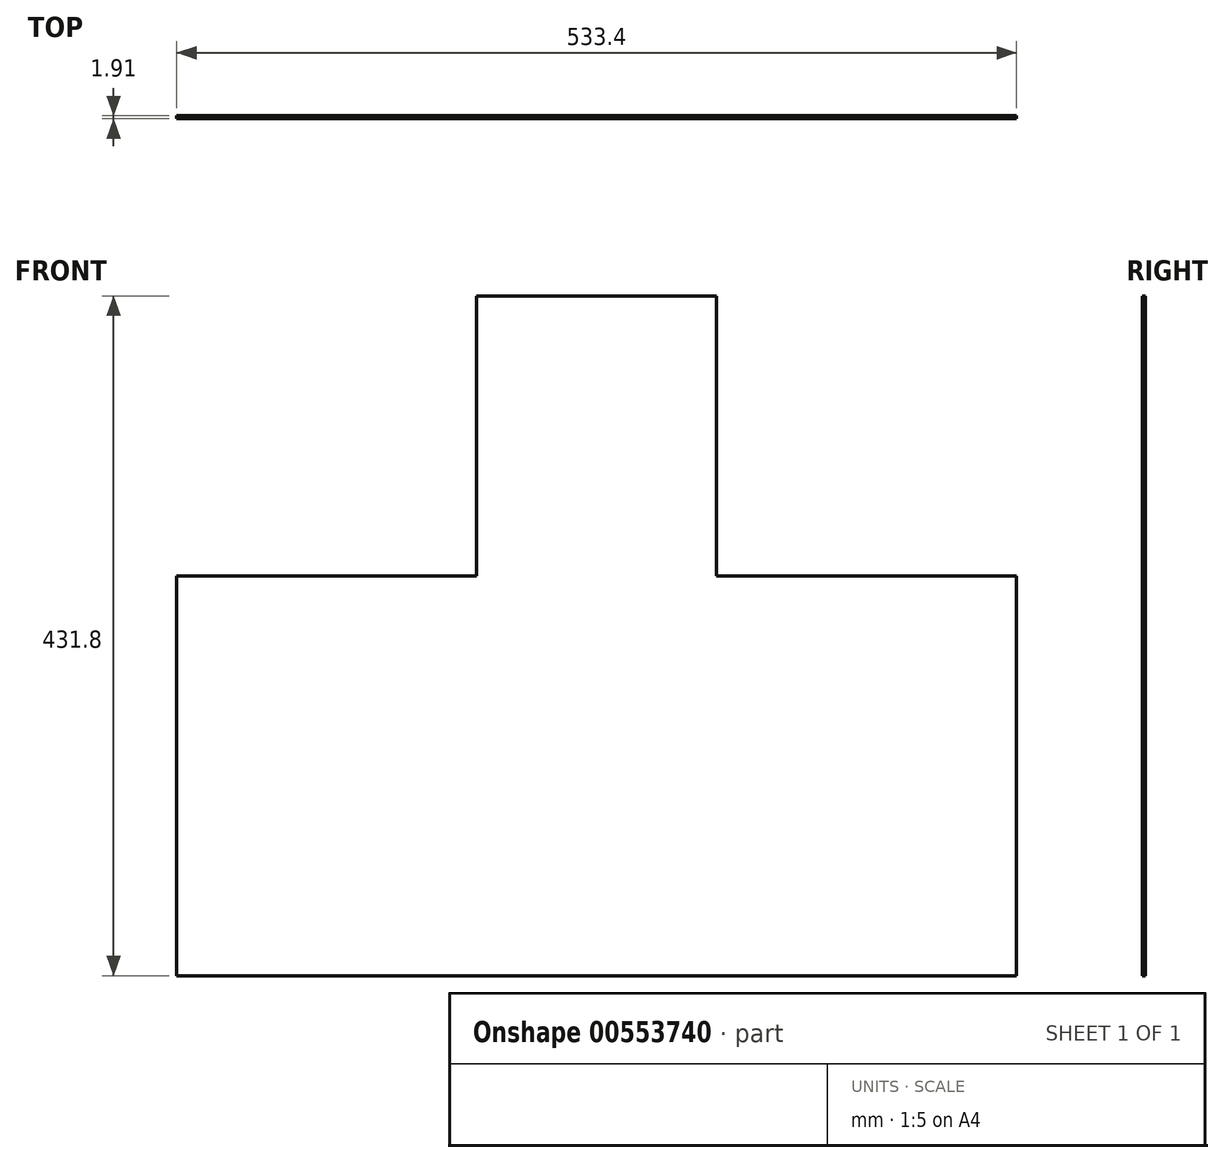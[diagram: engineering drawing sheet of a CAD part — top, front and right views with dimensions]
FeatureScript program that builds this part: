
annotation { "Feature Type Name" : "Feature", "Feature Type Description" : "" }
export const myFeature = defineFeature(function(context is Context, id is Id, definition is map)
    precondition{}
    {
        {
            var Q0;
            Q0=qCreatedBy(makeId("Front.planeOp"),FACE);
            var sketch = newSketch(context, id + "F0", { "sketchPlane" : qUnion([Q0])});
            skLineSegment(sketch, "E0", {"start": v(-275.39, -210.45) * mm, "end": v(258.01, -210.45) * mm});
            skLineSegment(sketch, "E1", {"start": v(258.01, -210.45) * mm, "end": v(258.01, 43.55) * mm});
            skLineSegment(sketch, "E2", {"start": v(258.01, 43.55) * mm, "end": v(67.51, 43.55) * mm});
            skLineSegment(sketch, "E3", {"start": v(67.51, 43.55) * mm, "end": v(67.51, 221.35) * mm});
            skLineSegment(sketch, "E4", {"start": v(67.51, 221.35) * mm, "end": v(-84.89, 221.35) * mm});
            skLineSegment(sketch, "E5", {"start": v(-84.89, 221.35) * mm, "end": v(-84.89, 43.55) * mm});
            skLineSegment(sketch, "E6", {"start": v(-84.89, 43.55) * mm, "end": v(-275.39, 43.55) * mm});
            skLineSegment(sketch, "E7", {"start": v(-275.39, 43.55) * mm, "end": v(-275.39, -210.45) * mm});
            skLineSegment(sketch, "E8.0", {"start": v(65.6, 219.44) * mm, "end": v(-82.98, 219.44) * mm});
            skLineSegment(sketch, "E8.1", {"start": v(65.6, 41.64) * mm, "end": v(65.6, 219.44) * mm});
            skLineSegment(sketch, "E8.2", {"start": v(-82.98, 219.44) * mm, "end": v(-82.98, 41.64) * mm});
            skLineSegment(sketch, "E8.3", {"start": v(256.1, 41.64) * mm, "end": v(65.6, 41.64) * mm});
            skLineSegment(sketch, "E8.4", {"start": v(-82.98, 41.64) * mm, "end": v(-273.48, 41.64) * mm});
            skLineSegment(sketch, "E8.5", {"start": v(-273.48, 41.64) * mm, "end": v(-273.48, -208.55) * mm});
            skLineSegment(sketch, "E8.6", {"start": v(-273.48, -208.55) * mm, "end": v(256.1, -208.55) * mm});
            skLineSegment(sketch, "E8.7", {"start": v(256.1, -208.55) * mm, "end": v(256.1, 41.64) * mm});
            skSolve(sketch);
        }
        {
            var Q0;
            Q0=makeQuery(id+"F0.imprint","IMPRINT",FACE,{"disambiguationData":[TD([[makeQuery(id+"F0.imprint","IMPRINT",EDGE,{"derivedFrom":sQuery(id+"F0.wireOp",EDGE,"E0")}),1.0]])]});
            extrude(context, id + "F1", {"entities" : qUnion([Q0]), "depth" : 1.9 * mm, "offsetDistance" : 25.4 * mm});
        }
        {
            var Q0;
            Q0 = qSketchRegion(id + "F0", true);
            var Q1;
            Q1=makeQuery(id+"F0.imprint","IMPRINT",FACE,{"disambiguationData":[TD([[makeQuery(id+"F0.imprint","IMPRINT",EDGE,{"derivedFrom":sQuery(id+"F0.wireOp",EDGE,"E8.0")}),1.0]])]});
            extrude(context, id + "F2", {"entities" : qUnion([Q0, Q1]), "operationType" : NewBodyOperationType.ADD, "depth" : 1.9 * mm, "offsetDistance" : 25.4 * mm});
        }
    });
